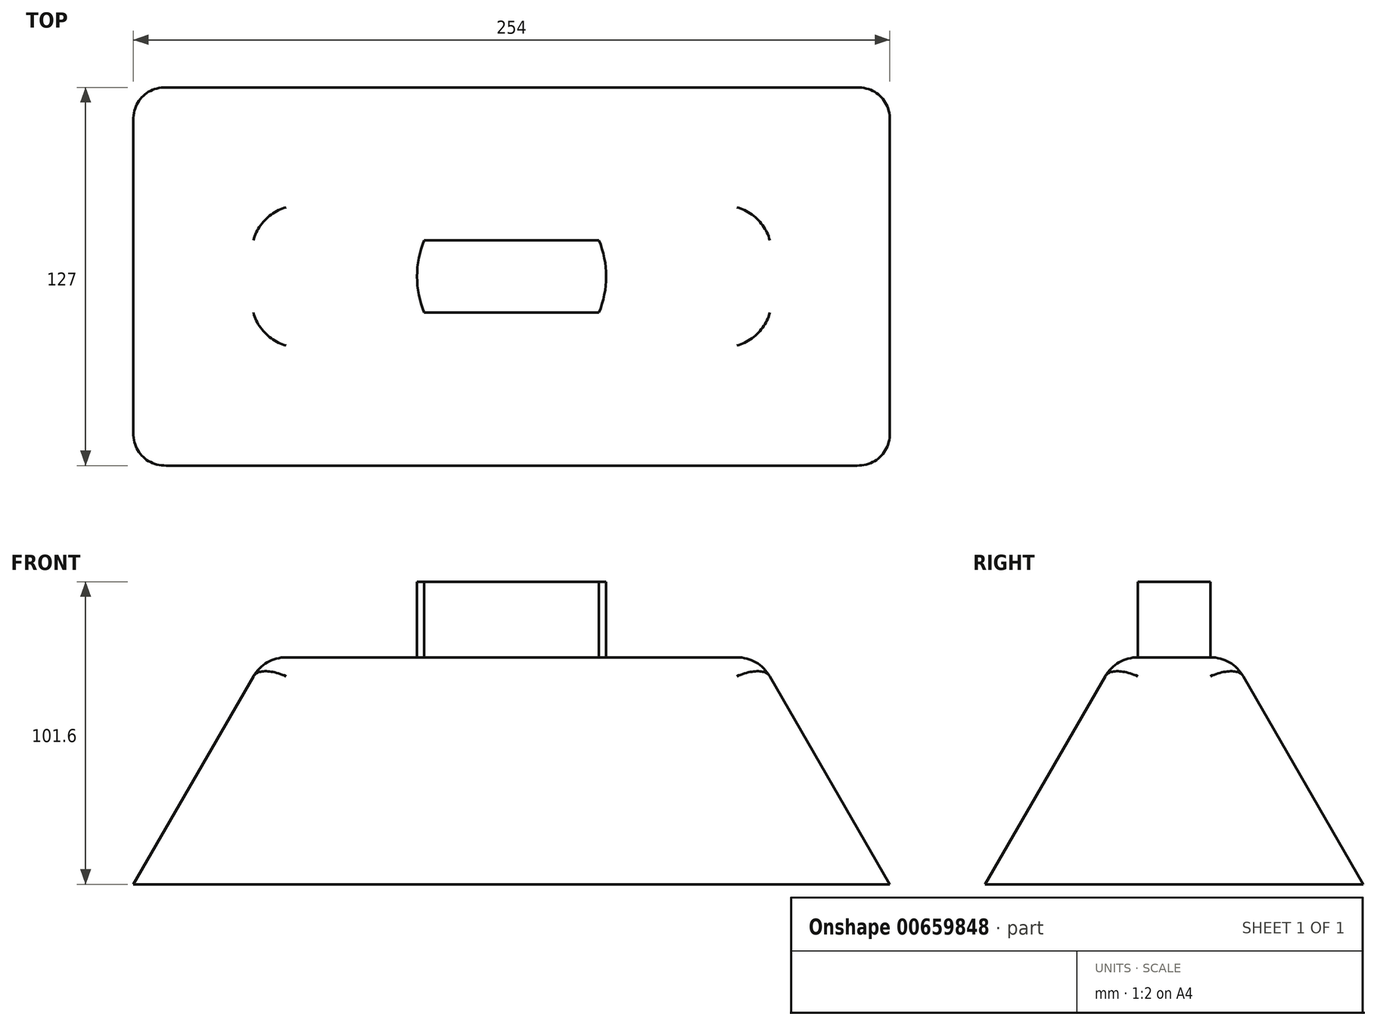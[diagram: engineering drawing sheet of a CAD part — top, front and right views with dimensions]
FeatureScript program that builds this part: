
annotation { "Feature Type Name" : "Feature", "Feature Type Description" : "" }
export const myFeature = defineFeature(function(context is Context, id is Id, definition is map)
    precondition{}
    {
        {
            var Q0;
            Q0=qCreatedBy(makeId("Top.planeOp"),FACE);
            var sketch = newSketch(context, id + "F0", { "sketchPlane" : qUnion([Q0])});
            skLineSegment(sketch, "E0.bottom", {"start": v(127, 63.5) * mm, "end": v(-127, 63.5) * mm});
            skLineSegment(sketch, "E0.top", {"start": v(127, -63.5) * mm, "end": v(-127, -63.5) * mm});
            skLineSegment(sketch, "E0.left", {"start": v(127, 63.5) * mm, "end": v(127, -63.5) * mm});
            skLineSegment(sketch, "E0.right", {"start": v(-127, 63.5) * mm, "end": v(-127, -63.5) * mm});
            skPoint(sketch, "E0.middle", {"position": v(0, 0) * mm});
            skSolve(sketch);
        }
        {
            var Q0;
            Q0=makeQuery(id+"F0.imprint","IMPRINT",FACE,{"disambiguationData":[TD([[makeQuery(id+"F0.imprint","IMPRINT",EDGE,{"derivedFrom":sQuery(id+"F0.wireOp",EDGE,"E0.bottom")}),1.0]])]});
            extrude(context, id + "F1", {"entities" : qUnion([Q0]), "depth" : 76.2 * mm, "offsetDistance" : 25.4 * mm, "hasDraft" : true, "draftAngle" : 30 * degree, "draftPullDirection" : true});
        }
        {
            var Q0;
            Q0=makeQuery(id+"F1.opExtrude","CAP_FACE",FACE,{"disambiguationData":[OSD([sQuery(id+"F0.wireOp",EDGE,"E0.bottom"),sQuery(id+"F0.wireOp",EDGE,"E0.top"),sQuery(id+"F0.wireOp",EDGE,"E0.left"),sQuery(id+"F0.wireOp",EDGE,"E0.right")])],"isStart":false});
            var Q1;
            Q1=makeQuery(id+"F1.opExtrude","SWEPT_EDGE",EDGE,{"disambiguationData":[OSD([sQuery(id+"F0.wireOp",EDGE,"E0.bottom"),sQuery(id+"F0.wireOp",EDGE,"E0.left")])]});
            var Q2;
            Q2=makeQuery(id+"F1.opExtrude","SWEPT_EDGE",EDGE,{"disambiguationData":[OSD([sQuery(id+"F0.wireOp",EDGE,"E0.top"),sQuery(id+"F0.wireOp",EDGE,"E0.left")])]});
            var Q3;
            Q3=makeQuery(id+"F1.opExtrude","SWEPT_EDGE",EDGE,{"disambiguationData":[OSD([sQuery(id+"F0.wireOp",EDGE,"E0.top"),sQuery(id+"F0.wireOp",EDGE,"E0.right")])]});
            var Q4;
            Q4=makeQuery(id+"F1.opExtrude","SWEPT_EDGE",EDGE,{"disambiguationData":[OSD([sQuery(id+"F0.wireOp",EDGE,"E0.bottom"),sQuery(id+"F0.wireOp",EDGE,"E0.right")])]});
            fillet(context, id + "F2", {"entities" : qUnion([Q0, Q1, Q2, Q3, Q4]), "radius" : 12.7 * mm, "tangentPropagation" : true, "allowEdgeOverflow" : false});
        }
        {
            var Q0;
            Q0=makeQuery(id+"F1.opExtrude","CAP_FACE",FACE,{"disambiguationData":[OSD([sQuery(id+"F0.wireOp",EDGE,"E0.bottom"),sQuery(id+"F0.wireOp",EDGE,"E0.top"),sQuery(id+"F0.wireOp",EDGE,"E0.left"),sQuery(id+"F0.wireOp",EDGE,"E0.right")])],"isStart":false});
            var sketch = newSketch(context, id + "F3", { "sketchPlane" : qUnion([Q0])});
            skCircle(sketch, "E1", {"center": v(0, 0) * mm, "radius": 31.75 * mm});
            skSolve(sketch);
        }
        {
            var Q0;
            {var subQ0=sQuery(id+"F3.wireOp",EDGE,"E1");var subQ1=sQuery(id+"F0.wireOp",EDGE,"E0.top");var subQ2=sQuery(id+"F0.wireOp",EDGE,"E0.bottom");var subQ3=makeQuery(id+"F1.opExtrude","CAP_FACE",FACE,{"disambiguationData":[OSD([subQ2,subQ1,sQuery(id+"F0.wireOp",EDGE,"E0.left"),sQuery(id+"F0.wireOp",EDGE,"E0.right")])],"isStart":false});var subQ4=makeQuery(id+"F2.opFillet","BLEND_EDGE",EDGE,{"blendedFrom":[makeQuery(id+"F1.opExtrude","CAP_EDGE",EDGE,{"disambiguationData":[OSD([subQ2])],"isStart":false}),subQ3],"blendedInto":[subQ3]});var subQ5=makeQuery(id+"F3.imprint","INTERSECT",VERTEX,{"disambiguationData":[OD(0.0)],"derivedFrom":[subQ4,subQ0]});Q0=makeQuery(id+"F3.imprint","IMPRINT",FACE,{"disambiguationData":[TD([[makeQuery(id+"F3.imprint","IMPRINT",EDGE,{"disambiguationData":[TD([[subQ5,-1.0]])],"derivedFrom":subQ0}),1.0]])]});}
            extrude(context, id + "F4", {"entities" : qUnion([Q0]), "operationType" : NewBodyOperationType.ADD, "depth" : 25.4 * mm, "offsetDistance" : 25.4 * mm});
        }
    });
